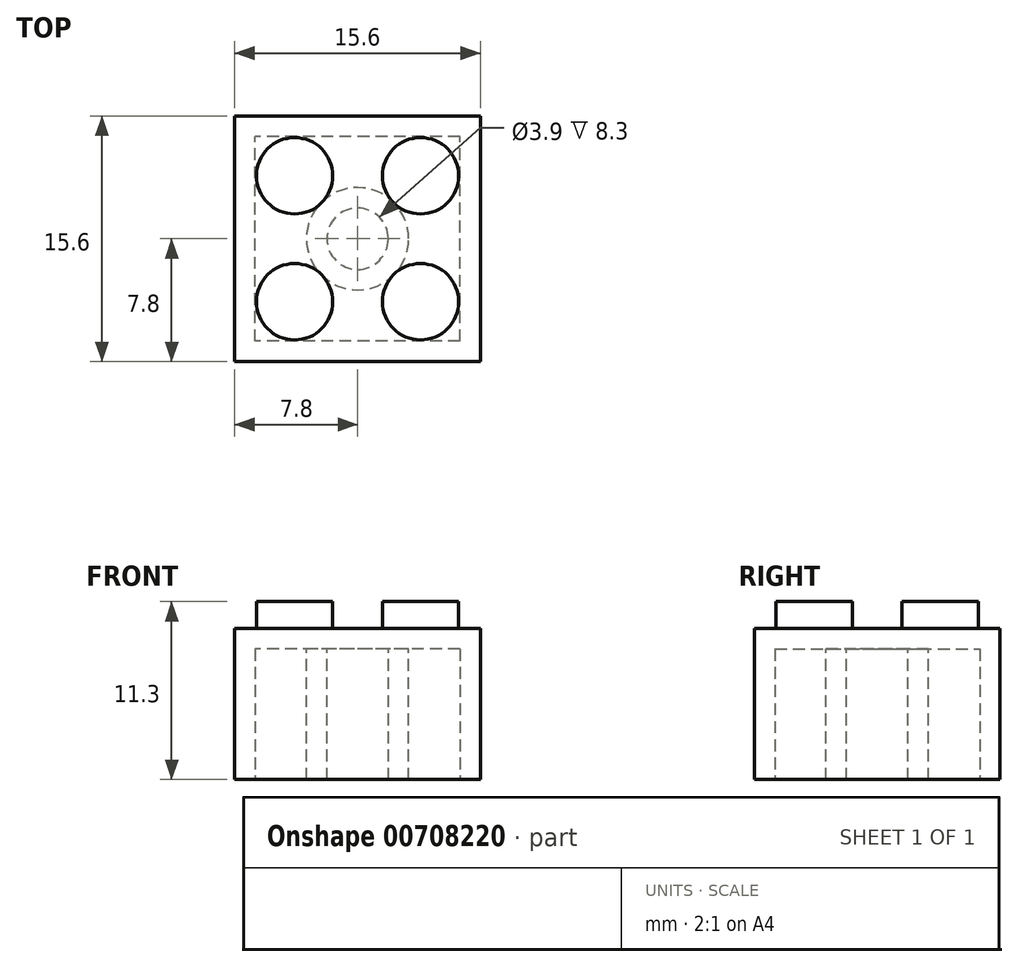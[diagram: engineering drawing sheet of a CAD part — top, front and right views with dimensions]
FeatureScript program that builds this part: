
annotation { "Feature Type Name" : "Feature", "Feature Type Description" : "" }
export const myFeature = defineFeature(function(context is Context, id is Id, definition is map)
    precondition{}
    {
        {
            var Q0;
            Q0=qCreatedBy(makeId("Top.planeOp"),FACE);
            var sketch = newSketch(context, id + "F0", { "sketchPlane" : qUnion([Q0])});
            skLineSegment(sketch, "E0.bottom", {"start": v(7.8, -7.8) * mm, "end": v(-7.8, -7.8) * mm});
            skLineSegment(sketch, "E0.top", {"start": v(7.8, 7.8) * mm, "end": v(-7.8, 7.8) * mm});
            skLineSegment(sketch, "E0.left", {"start": v(7.8, -7.8) * mm, "end": v(7.8, 7.8) * mm});
            skLineSegment(sketch, "E0.right", {"start": v(-7.8, -7.8) * mm, "end": v(-7.8, 7.8) * mm});
            skPoint(sketch, "E0.middle", {"position": v(0, 0) * mm});
            skSolve(sketch);
        }
        {
            var Q0;
            Q0=qSketchRegion(id+"F0",true);
            extrude(context, id + "F1", {"entities" : qUnion([Q0]), "depth" : 9.6 * mm, "offsetDistance" : 25 * mm});
        }
        {
            var Q0;
            Q0=makeQuery(id+"F1.opExtrude","CAP_FACE",FACE,{"disambiguationData":[OSD([sQuery(id+"F0.wireOp",EDGE,"E0.bottom"),sQuery(id+"F0.wireOp",EDGE,"E0.top"),sQuery(id+"F0.wireOp",EDGE,"E0.left"),sQuery(id+"F0.wireOp",EDGE,"E0.right")])],"isStart":true});
            shell(context, id + "F2", {"entities" : qUnion([Q0]), "thickness" : 1.3 * mm});
        }
        {
            var Q0;
            Q0=makeQuery(id+"F1.opExtrude","CAP_FACE",FACE,{"disambiguationData":[OSD([sQuery(id+"F0.wireOp",EDGE,"E0.bottom"),sQuery(id+"F0.wireOp",EDGE,"E0.top"),sQuery(id+"F0.wireOp",EDGE,"E0.left"),sQuery(id+"F0.wireOp",EDGE,"E0.right")])],"isStart":false});
            var sketch = newSketch(context, id + "F3", { "sketchPlane" : qUnion([Q0])});
            skCircle(sketch, "E1", {"center": v(-4, 4) * mm, "radius": 2.43 * mm});
            skCircle(sketch, "E2.MirrorC", {"center": v(4, 4) * mm, "radius": 2.43 * mm});
            skCircle(sketch, "E3.MirrorC", {"center": v(-4, -4) * mm, "radius": 2.43 * mm});
            skCircle(sketch, "E4.MirrorC", {"center": v(4, -4) * mm, "radius": 2.43 * mm});
            skSolve(sketch);
        }
        {
            var Q0;
            Q0=qSketchRegion(id+"F3",true);
            extrude(context, id + "F4", {"entities" : qUnion([Q0]), "operationType" : NewBodyOperationType.ADD, "depth" : 1.7 * mm, "offsetDistance" : 25 * mm});
        }
        {
            var Q0;
            Q0=makeQuery(id+"F2.opShell","OFFSET_FACE",FACE,{"disambiguationData":[OSD([sQuery(id+"F0.wireOp",EDGE,"E0.bottom"),sQuery(id+"F0.wireOp",EDGE,"E0.top"),sQuery(id+"F0.wireOp",EDGE,"E0.left"),sQuery(id+"F0.wireOp",EDGE,"E0.right")])]});
            var sketch = newSketch(context, id + "F5", { "sketchPlane" : qUnion([Q0])});
            skCircle(sketch, "E5", {"center": v(0, 0) * mm, "radius": 3.25 * mm});
            skSolve(sketch);
        }
        {
            var Q0;
            Q0=qSketchRegion(id+"F5",true);
            var Q1;
            Q1=makeQuery(id+"F1.opExtrude","CAP_FACE",FACE,{"disambiguationData":[OSD([sQuery(id+"F0.wireOp",EDGE,"E0.bottom"),sQuery(id+"F0.wireOp",EDGE,"E0.top"),sQuery(id+"F0.wireOp",EDGE,"E0.left"),sQuery(id+"F0.wireOp",EDGE,"E0.right")])],"isStart":true});
            extrude(context, id + "F6", {"entities" : qUnion([Q0]), "operationType" : NewBodyOperationType.ADD, "endBound" : BoundingType.UP_TO_SURFACE, "depth" : 25 * mm, "endBoundEntityFace" : qUnion([Q1]), "offsetDistance" : 25 * mm});
        }
        {
            var Q0;
            Q0=makeQuery(id+"F6.opExtrude","CAP_FACE",FACE,{"disambiguationData":[OSD([sQuery(id+"F5.wireOp",EDGE,"E5")])],"isStart":false});
            shell(context, id + "F7", {"entities" : qUnion([Q0]), "thickness" : 1.3 * mm});
        }
    });
